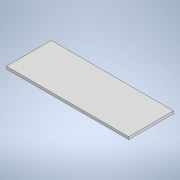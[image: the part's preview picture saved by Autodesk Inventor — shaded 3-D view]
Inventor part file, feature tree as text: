
AUTODESK INVENTOR PART (.ipt)
format: ipt  version: 2021 (Build 250183000, 183)  size: 91,648 bytes
history: native  units: mm
features: extrude x1, sketch x1
ambient origin geometry x8: Origin, YZ Plane, XZ Plane, XY Plane, X Axis, Y Axis, Z Axis, Center Point
bodies: Solid1 (feature_tree)
feature tree (2):
  extrude  "Extrusion1"  Depth=88.0mm
  sketch  "Sketch1"  dims[d0=240.0mm d1=88.0mm d2=5.0mm d3=0.0mm]
